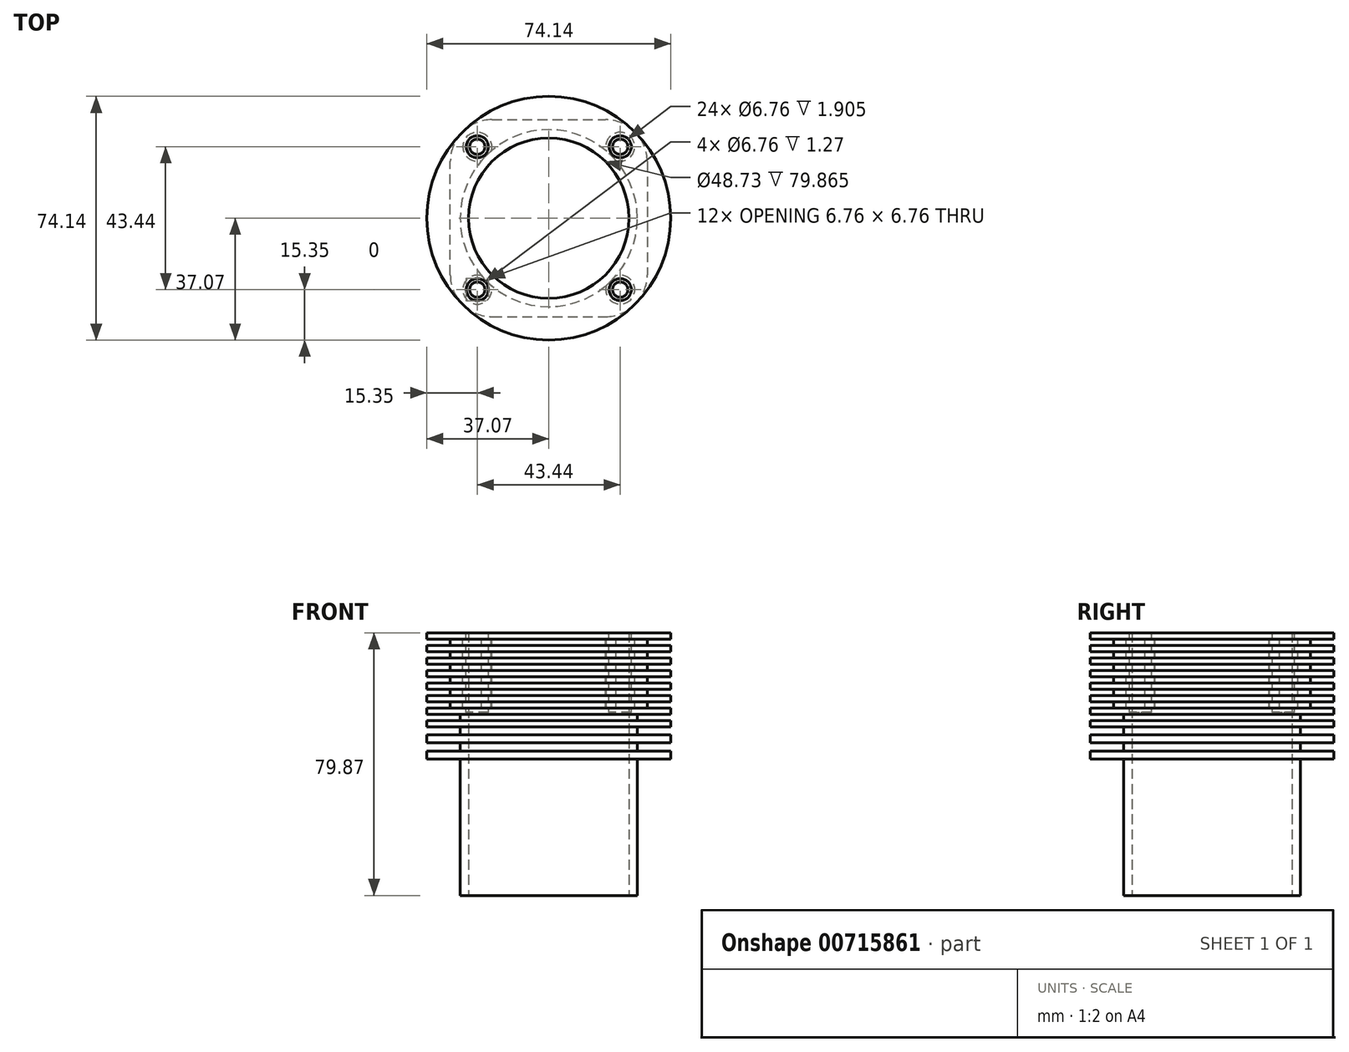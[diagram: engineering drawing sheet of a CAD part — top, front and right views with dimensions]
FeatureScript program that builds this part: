
annotation { "Feature Type Name" : "Feature", "Feature Type Description" : "" }
export const myFeature = defineFeature(function(context is Context, id is Id, definition is map)
    precondition{}
    {
        {
            var Q0;
            Q0=qCreatedBy(makeId("Front.planeOp"),FACE);
            var sketch = newSketch(context, id + "F0", { "sketchPlane" : qUnion([Q0])});
            skLineSegment(sketch, "E0", {"start": v(24.37, -35.45) * mm, "end": v(24.37, 44.42) * mm});
            skLineSegment(sketch, "E1", {"start": v(24.37, 44.42) * mm, "end": v(37.07, 44.42) * mm});
            skLineSegment(sketch, "E2", {"start": v(37.07, 42.51) * mm, "end": v(26.9, 42.51) * mm});
            skLineSegment(sketch, "E3", {"start": v(26.9, 42.51) * mm, "end": v(26.9, 40.6) * mm});
            skLineSegment(sketch, "E4", {"start": v(37.07, 42.51) * mm, "end": v(37.07, 44.42) * mm});
            skLineSegment(sketch, "E5", {"start": v(26.9, 40.6) * mm, "end": v(37.07, 40.6) * mm});
            skLineSegment(sketch, "E6", {"start": v(37.07, 40.6) * mm, "end": v(37.07, 38.7) * mm});
            skLineSegment(sketch, "E7", {"start": v(37.07, 38.7) * mm, "end": v(26.9, 38.7) * mm});
            skLineSegment(sketch, "E8", {"start": v(26.9, 38.7) * mm, "end": v(26.9, 36.8) * mm});
            skLineSegment(sketch, "E9", {"start": v(26.9, 36.8) * mm, "end": v(37.07, 36.8) * mm});
            skLineSegment(sketch, "E10", {"start": v(37.07, 36.8) * mm, "end": v(37.07, 34.9) * mm});
            skLineSegment(sketch, "E11", {"start": v(37.07, 34.9) * mm, "end": v(26.9, 34.9) * mm});
            skLineSegment(sketch, "E12", {"start": v(26.9, 34.9) * mm, "end": v(26.9, 32.99) * mm});
            skLineSegment(sketch, "E13", {"start": v(26.9, 32.99) * mm, "end": v(37.07, 32.99) * mm});
            skLineSegment(sketch, "E14", {"start": v(37.07, 32.99) * mm, "end": v(37.07, 31.08) * mm});
            skLineSegment(sketch, "E15", {"start": v(37.07, 31.08) * mm, "end": v(26.9, 31.08) * mm});
            skLineSegment(sketch, "E16", {"start": v(26.9, 31.08) * mm, "end": v(26.9, 29.18) * mm});
            skLineSegment(sketch, "E17", {"start": v(26.9, 29.18) * mm, "end": v(37.07, 29.18) * mm});
            skLineSegment(sketch, "E18", {"start": v(37.07, 29.18) * mm, "end": v(37.07, 27.27) * mm});
            skLineSegment(sketch, "E19", {"start": v(37.07, 27.27) * mm, "end": v(26.9, 27.27) * mm});
            skLineSegment(sketch, "E20", {"start": v(26.9, 27.27) * mm, "end": v(26.9, 25.37) * mm});
            skLineSegment(sketch, "E21", {"start": v(26.9, 25.37) * mm, "end": v(37.07, 25.37) * mm});
            skLineSegment(sketch, "E22", {"start": v(37.07, 25.37) * mm, "end": v(37.07, 23.46) * mm});
            skLineSegment(sketch, "E23", {"start": v(37.07, 23.46) * mm, "end": v(26.9, 23.46) * mm});
            skLineSegment(sketch, "E24", {"start": v(26.9, 23.46) * mm, "end": v(26.9, 21.56) * mm});
            skLineSegment(sketch, "E25", {"start": v(26.9, 21.56) * mm, "end": v(37.07, 21.56) * mm});
            skLineSegment(sketch, "E26", {"start": v(37.07, 21.56) * mm, "end": v(37.07, 19.65) * mm});
            skLineSegment(sketch, "E27", {"start": v(37.07, 19.65) * mm, "end": v(26.9, 19.65) * mm});
            skLineSegment(sketch, "E28", {"start": v(26.9, 19.65) * mm, "end": v(26.9, 17.75) * mm});
            skLineSegment(sketch, "E29", {"start": v(26.9, 17.75) * mm, "end": v(37.07, 17.75) * mm});
            skLineSegment(sketch, "E30", {"start": v(37.07, 17.75) * mm, "end": v(37.07, 15.84) * mm});
            skLineSegment(sketch, "E31", {"start": v(37.07, 15.84) * mm, "end": v(26.9, 15.84) * mm});
            skLineSegment(sketch, "E32", {"start": v(26.9, 15.84) * mm, "end": v(26.9, 13.38) * mm});
            skLineSegment(sketch, "E33", {"start": v(26.9, 13.38) * mm, "end": v(37.07, 13.38) * mm});
            skLineSegment(sketch, "E34", {"start": v(37.07, 13.38) * mm, "end": v(37.07, 10.93) * mm});
            skLineSegment(sketch, "E35", {"start": v(37.07, 10.93) * mm, "end": v(26.9, 10.93) * mm});
            skLineSegment(sketch, "E36", {"start": v(26.9, 10.93) * mm, "end": v(26.9, 8.47) * mm});
            skLineSegment(sketch, "E37", {"start": v(26.9, 8.47) * mm, "end": v(37.07, 8.47) * mm});
            skLineSegment(sketch, "E38", {"start": v(37.07, 8.47) * mm, "end": v(37.07, 6.02) * mm});
            skLineSegment(sketch, "E39", {"start": v(37.07, 6.02) * mm, "end": v(26.9, 6.02) * mm});
            skLineSegment(sketch, "E40", {"start": v(26.9, 6.02) * mm, "end": v(26.9, -35.45) * mm});
            skLineSegment(sketch, "E41", {"start": v(26.9, -35.45) * mm, "end": v(24.37, -35.45) * mm});
            skLineSegment(sketch, "E42", {"start": v(0, -13.6) * mm, "end": v(0, 23.15) * mm});
            skSolve(sketch);
        }
        {
            var Q0;
            Q0=makeQuery(id+"F0.imprint","IMPRINT",FACE,{"disambiguationData":[TD([[makeQuery(id+"F0.imprint","IMPRINT",EDGE,{"derivedFrom":sQuery(id+"F0.wireOp",EDGE,"E0")}),-1.0]])]});
            var Q1;
            Q1=sQuery(id+"F0.wireOp",EDGE,"E42");
            revolve(context, id + "F1", {"surfaceOperationType" : NewSurfaceOperationType.NEW, "entities" : qUnion([Q0]), "axis" : qUnion([Q1]), "revolveType" : RevolveType.FULL});
        }
        {
            var Q0;
            Q0=makeQuery(id+"F1.opRevolve","SWEPT_FACE",FACE,{"disambiguationData":[OSD([sQuery(id+"F0.wireOp",EDGE,"E1")])]});
            var sketch = newSketch(context, id + "F2", { "sketchPlane" : qUnion([Q0])});
            skLineSegment(sketch, "E43.bottom", {"start": v(17.23, 29.93) * mm, "end": v(-17.23, 29.93) * mm});
            skLineSegment(sketch, "E43.top", {"start": v(17.23, -29.93) * mm, "end": v(-17.23, -29.93) * mm});
            skLineSegment(sketch, "E43.left", {"start": v(29.93, 17.23) * mm, "end": v(29.93, -17.23) * mm});
            skLineSegment(sketch, "E43.right", {"start": v(-29.93, 17.23) * mm, "end": v(-29.93, -17.23) * mm});
            skPoint(sketch, "E43.middle", {"position": v(0, 0) * mm});
            skPoint(sketch, "E44.visualSharp", {"position": v(-29.93, 29.93) * mm});
            skArc(sketch, "E44.filletArc", {"start": v(-17.23, 29.93) * mm, "mid": v(-26.21, 26.21) * mm, "end": v(-29.93, 17.23) * mm});
            skPoint(sketch, "E45.visualSharp", {"position": v(29.93, 29.93) * mm});
            skArc(sketch, "E45.filletArc", {"start": v(29.93, 17.23) * mm, "mid": v(26.21, 26.21) * mm, "end": v(17.23, 29.93) * mm});
            skPoint(sketch, "E46.visualSharp", {"position": v(29.93, -29.93) * mm});
            skArc(sketch, "E46.filletArc", {"start": v(17.23, -29.93) * mm, "mid": v(26.21, -26.21) * mm, "end": v(29.93, -17.23) * mm});
            skPoint(sketch, "E47.visualSharp", {"position": v(-29.93, -29.93) * mm});
            skArc(sketch, "E47.filletArc", {"start": v(-29.93, -17.23) * mm, "mid": v(-26.21, -26.21) * mm, "end": v(-17.23, -29.93) * mm});
            skCircle(sketch, "E48", {"center": v(-21.72, 21.72) * mm, "radius": 4.41 * mm});
            skCircle(sketch, "E49.MirrorC", {"center": v(21.72, 21.72) * mm, "radius": 4.41 * mm});
            skCircle(sketch, "E50.MirrorC", {"center": v(-21.72, -21.72) * mm, "radius": 4.41 * mm});
            skCircle(sketch, "E51.MirrorC", {"center": v(21.72, -21.72) * mm, "radius": 4.41 * mm});
            skSolve(sketch);
        }
        {
            var Q0;
            {var subQ7=sQuery(id+"F2.wireOp",EDGE,"E43.bottom");Q0=makeQuery(id+"F2.imprint","IMPRINT",FACE,{"disambiguationData":[TD([[makeQuery(id+"F2.imprint","IMPRINT",EDGE,{"derivedFrom":subQ7}),1.0]])]});}
            extrude(context, id + "F3", {"entities" : qUnion([Q0]), "operationType" : NewBodyOperationType.ADD, "oppositeDirection" : true, "depth" : 24.13 * mm, "offsetDistance" : 25.4 * mm});
        }
        {
            var Q0;
            Q0=sQuery(id+"F2.wireOp",VERTEX,"E50.MirrorC.center");
            var Q1;
            Q1=makeQuery(id+"F1.opRevolve","SWEPT_BODY",BODY,{"disambiguationData":[OSD([sQuery(id+"F0.wireOp",EDGE,"E0"),sQuery(id+"F0.wireOp",EDGE,"E1"),sQuery(id+"F0.wireOp",EDGE,"E2"),sQuery(id+"F0.wireOp",EDGE,"E3"),sQuery(id+"F0.wireOp",EDGE,"E4"),sQuery(id+"F0.wireOp",EDGE,"E5"),sQuery(id+"F0.wireOp",EDGE,"E6"),sQuery(id+"F0.wireOp",EDGE,"E7"),sQuery(id+"F0.wireOp",EDGE,"E8"),sQuery(id+"F0.wireOp",EDGE,"E9"),sQuery(id+"F0.wireOp",EDGE,"E10"),sQuery(id+"F0.wireOp",EDGE,"E11"),sQuery(id+"F0.wireOp",EDGE,"E12"),sQuery(id+"F0.wireOp",EDGE,"E13"),sQuery(id+"F0.wireOp",EDGE,"E14"),sQuery(id+"F0.wireOp",EDGE,"E15"),sQuery(id+"F0.wireOp",EDGE,"E16"),sQuery(id+"F0.wireOp",EDGE,"E17"),sQuery(id+"F0.wireOp",EDGE,"E18"),sQuery(id+"F0.wireOp",EDGE,"E19"),sQuery(id+"F0.wireOp",EDGE,"E20"),sQuery(id+"F0.wireOp",EDGE,"E21"),sQuery(id+"F0.wireOp",EDGE,"E22"),sQuery(id+"F0.wireOp",EDGE,"E23"),sQuery(id+"F0.wireOp",EDGE,"E24"),sQuery(id+"F0.wireOp",EDGE,"E25"),sQuery(id+"F0.wireOp",EDGE,"E26"),sQuery(id+"F0.wireOp",EDGE,"E27"),sQuery(id+"F0.wireOp",EDGE,"E28"),sQuery(id+"F0.wireOp",EDGE,"E29"),sQuery(id+"F0.wireOp",EDGE,"E30"),sQuery(id+"F0.wireOp",EDGE,"E31"),sQuery(id+"F0.wireOp",EDGE,"E32"),sQuery(id+"F0.wireOp",EDGE,"E33"),sQuery(id+"F0.wireOp",EDGE,"E34"),sQuery(id+"F0.wireOp",EDGE,"E35"),sQuery(id+"F0.wireOp",EDGE,"E36"),sQuery(id+"F0.wireOp",EDGE,"E37"),sQuery(id+"F0.wireOp",EDGE,"E38"),sQuery(id+"F0.wireOp",EDGE,"E39"),sQuery(id+"F0.wireOp",EDGE,"E40"),sQuery(id+"F0.wireOp",EDGE,"E41")])]});
            hole(context, id + "F4", {"style" : HoleStyle.SIMPLE, "endStyle" : HoleEndStyle.BLIND, "standardTappedOrClearance" : lookupTablePath({ "standard" : "ANSI", "fit" : "Normal (ASME)", "size" : "1/4", "type" : "Clearance" }), "standardBlindInLast" : lookupTablePath({ "fit" : "Free", "standard" : "ANSI", "size" : "1/4", "type" : "Clearance" }), "holeDiameter" : 6.76 * mm, "majorDiameter" : 6.35 * mm, "holeDepth" : 24.13 * mm, "isTappedThrough" : true, "tappedDepth" : 12.7 * mm, "tapClearance" : 3, "startFromSketch" : true, "locations" : qUnion([Q0]), "scope" : qUnion([Q1])});
        }
        {
            var Q0;
            Q0=sQuery(id+"F2.wireOp",VERTEX,"E51.MirrorC.center");
            var Q1;
            Q1=makeQuery(id+"F1.opRevolve","SWEPT_BODY",BODY,{"disambiguationData":[OSD([sQuery(id+"F0.wireOp",EDGE,"E0"),sQuery(id+"F0.wireOp",EDGE,"E1"),sQuery(id+"F0.wireOp",EDGE,"E2"),sQuery(id+"F0.wireOp",EDGE,"E3"),sQuery(id+"F0.wireOp",EDGE,"E4"),sQuery(id+"F0.wireOp",EDGE,"E5"),sQuery(id+"F0.wireOp",EDGE,"E6"),sQuery(id+"F0.wireOp",EDGE,"E7"),sQuery(id+"F0.wireOp",EDGE,"E8"),sQuery(id+"F0.wireOp",EDGE,"E9"),sQuery(id+"F0.wireOp",EDGE,"E10"),sQuery(id+"F0.wireOp",EDGE,"E11"),sQuery(id+"F0.wireOp",EDGE,"E12"),sQuery(id+"F0.wireOp",EDGE,"E13"),sQuery(id+"F0.wireOp",EDGE,"E14"),sQuery(id+"F0.wireOp",EDGE,"E15"),sQuery(id+"F0.wireOp",EDGE,"E16"),sQuery(id+"F0.wireOp",EDGE,"E17"),sQuery(id+"F0.wireOp",EDGE,"E18"),sQuery(id+"F0.wireOp",EDGE,"E19"),sQuery(id+"F0.wireOp",EDGE,"E20"),sQuery(id+"F0.wireOp",EDGE,"E21"),sQuery(id+"F0.wireOp",EDGE,"E22"),sQuery(id+"F0.wireOp",EDGE,"E23"),sQuery(id+"F0.wireOp",EDGE,"E24"),sQuery(id+"F0.wireOp",EDGE,"E25"),sQuery(id+"F0.wireOp",EDGE,"E26"),sQuery(id+"F0.wireOp",EDGE,"E27"),sQuery(id+"F0.wireOp",EDGE,"E28"),sQuery(id+"F0.wireOp",EDGE,"E29"),sQuery(id+"F0.wireOp",EDGE,"E30"),sQuery(id+"F0.wireOp",EDGE,"E31"),sQuery(id+"F0.wireOp",EDGE,"E32"),sQuery(id+"F0.wireOp",EDGE,"E33"),sQuery(id+"F0.wireOp",EDGE,"E34"),sQuery(id+"F0.wireOp",EDGE,"E35"),sQuery(id+"F0.wireOp",EDGE,"E36"),sQuery(id+"F0.wireOp",EDGE,"E37"),sQuery(id+"F0.wireOp",EDGE,"E38"),sQuery(id+"F0.wireOp",EDGE,"E39"),sQuery(id+"F0.wireOp",EDGE,"E40"),sQuery(id+"F0.wireOp",EDGE,"E41")])]});
            hole(context, id + "F5", {"style" : HoleStyle.SIMPLE, "endStyle" : HoleEndStyle.BLIND, "standardTappedOrClearance" : lookupTablePath({ "standard" : "ANSI", "fit" : "Normal (ASME)", "size" : "1/4", "type" : "Clearance" }), "standardBlindInLast" : lookupTablePath({ "fit" : "Free", "standard" : "ANSI", "size" : "1/4", "type" : "Clearance" }), "holeDiameter" : 6.76 * mm, "majorDiameter" : 6.35 * mm, "holeDepth" : 24.13 * mm, "isTappedThrough" : true, "tappedDepth" : 12.7 * mm, "tapClearance" : 3, "startFromSketch" : true, "locations" : qUnion([Q0]), "scope" : qUnion([Q1])});
        }
        {
            var Q0;
            Q0=sQuery(id+"F2.wireOp",VERTEX,"E49.MirrorC.center");
            var Q1;
            Q1=makeQuery(id+"F1.opRevolve","SWEPT_BODY",BODY,{"disambiguationData":[OSD([sQuery(id+"F0.wireOp",EDGE,"E0"),sQuery(id+"F0.wireOp",EDGE,"E1"),sQuery(id+"F0.wireOp",EDGE,"E2"),sQuery(id+"F0.wireOp",EDGE,"E3"),sQuery(id+"F0.wireOp",EDGE,"E4"),sQuery(id+"F0.wireOp",EDGE,"E5"),sQuery(id+"F0.wireOp",EDGE,"E6"),sQuery(id+"F0.wireOp",EDGE,"E7"),sQuery(id+"F0.wireOp",EDGE,"E8"),sQuery(id+"F0.wireOp",EDGE,"E9"),sQuery(id+"F0.wireOp",EDGE,"E10"),sQuery(id+"F0.wireOp",EDGE,"E11"),sQuery(id+"F0.wireOp",EDGE,"E12"),sQuery(id+"F0.wireOp",EDGE,"E13"),sQuery(id+"F0.wireOp",EDGE,"E14"),sQuery(id+"F0.wireOp",EDGE,"E15"),sQuery(id+"F0.wireOp",EDGE,"E16"),sQuery(id+"F0.wireOp",EDGE,"E17"),sQuery(id+"F0.wireOp",EDGE,"E18"),sQuery(id+"F0.wireOp",EDGE,"E19"),sQuery(id+"F0.wireOp",EDGE,"E20"),sQuery(id+"F0.wireOp",EDGE,"E21"),sQuery(id+"F0.wireOp",EDGE,"E22"),sQuery(id+"F0.wireOp",EDGE,"E23"),sQuery(id+"F0.wireOp",EDGE,"E24"),sQuery(id+"F0.wireOp",EDGE,"E25"),sQuery(id+"F0.wireOp",EDGE,"E26"),sQuery(id+"F0.wireOp",EDGE,"E27"),sQuery(id+"F0.wireOp",EDGE,"E28"),sQuery(id+"F0.wireOp",EDGE,"E29"),sQuery(id+"F0.wireOp",EDGE,"E30"),sQuery(id+"F0.wireOp",EDGE,"E31"),sQuery(id+"F0.wireOp",EDGE,"E32"),sQuery(id+"F0.wireOp",EDGE,"E33"),sQuery(id+"F0.wireOp",EDGE,"E34"),sQuery(id+"F0.wireOp",EDGE,"E35"),sQuery(id+"F0.wireOp",EDGE,"E36"),sQuery(id+"F0.wireOp",EDGE,"E37"),sQuery(id+"F0.wireOp",EDGE,"E38"),sQuery(id+"F0.wireOp",EDGE,"E39"),sQuery(id+"F0.wireOp",EDGE,"E40"),sQuery(id+"F0.wireOp",EDGE,"E41")])]});
            hole(context, id + "F6", {"style" : HoleStyle.SIMPLE, "endStyle" : HoleEndStyle.BLIND, "standardTappedOrClearance" : lookupTablePath({ "standard" : "ANSI", "fit" : "Normal (ASME)", "size" : "1/4", "type" : "Clearance" }), "standardBlindInLast" : lookupTablePath({ "fit" : "Free", "standard" : "ANSI", "size" : "1/4", "type" : "Clearance" }), "holeDiameter" : 6.76 * mm, "majorDiameter" : 6.35 * mm, "holeDepth" : 24.13 * mm, "isTappedThrough" : true, "tappedDepth" : 12.7 * mm, "tapClearance" : 3, "startFromSketch" : true, "locations" : qUnion([Q0]), "scope" : qUnion([Q1])});
        }
        {
            var Q0;
            Q0=sQuery(id+"F2.wireOp",VERTEX,"E48.center");
            var Q1;
            Q1=makeQuery(id+"F1.opRevolve","SWEPT_BODY",BODY,{"disambiguationData":[OSD([sQuery(id+"F0.wireOp",EDGE,"E0"),sQuery(id+"F0.wireOp",EDGE,"E1"),sQuery(id+"F0.wireOp",EDGE,"E2"),sQuery(id+"F0.wireOp",EDGE,"E3"),sQuery(id+"F0.wireOp",EDGE,"E4"),sQuery(id+"F0.wireOp",EDGE,"E5"),sQuery(id+"F0.wireOp",EDGE,"E6"),sQuery(id+"F0.wireOp",EDGE,"E7"),sQuery(id+"F0.wireOp",EDGE,"E8"),sQuery(id+"F0.wireOp",EDGE,"E9"),sQuery(id+"F0.wireOp",EDGE,"E10"),sQuery(id+"F0.wireOp",EDGE,"E11"),sQuery(id+"F0.wireOp",EDGE,"E12"),sQuery(id+"F0.wireOp",EDGE,"E13"),sQuery(id+"F0.wireOp",EDGE,"E14"),sQuery(id+"F0.wireOp",EDGE,"E15"),sQuery(id+"F0.wireOp",EDGE,"E16"),sQuery(id+"F0.wireOp",EDGE,"E17"),sQuery(id+"F0.wireOp",EDGE,"E18"),sQuery(id+"F0.wireOp",EDGE,"E19"),sQuery(id+"F0.wireOp",EDGE,"E20"),sQuery(id+"F0.wireOp",EDGE,"E21"),sQuery(id+"F0.wireOp",EDGE,"E22"),sQuery(id+"F0.wireOp",EDGE,"E23"),sQuery(id+"F0.wireOp",EDGE,"E24"),sQuery(id+"F0.wireOp",EDGE,"E25"),sQuery(id+"F0.wireOp",EDGE,"E26"),sQuery(id+"F0.wireOp",EDGE,"E27"),sQuery(id+"F0.wireOp",EDGE,"E28"),sQuery(id+"F0.wireOp",EDGE,"E29"),sQuery(id+"F0.wireOp",EDGE,"E30"),sQuery(id+"F0.wireOp",EDGE,"E31"),sQuery(id+"F0.wireOp",EDGE,"E32"),sQuery(id+"F0.wireOp",EDGE,"E33"),sQuery(id+"F0.wireOp",EDGE,"E34"),sQuery(id+"F0.wireOp",EDGE,"E35"),sQuery(id+"F0.wireOp",EDGE,"E36"),sQuery(id+"F0.wireOp",EDGE,"E37"),sQuery(id+"F0.wireOp",EDGE,"E38"),sQuery(id+"F0.wireOp",EDGE,"E39"),sQuery(id+"F0.wireOp",EDGE,"E40"),sQuery(id+"F0.wireOp",EDGE,"E41")])]});
            hole(context, id + "F7", {"style" : HoleStyle.SIMPLE, "endStyle" : HoleEndStyle.BLIND, "standardTappedOrClearance" : lookupTablePath({ "standard" : "ANSI", "fit" : "Normal (ASME)", "size" : "1/4", "type" : "Clearance" }), "standardBlindInLast" : lookupTablePath({ "fit" : "Free", "standard" : "ANSI", "size" : "1/4", "type" : "Clearance" }), "holeDiameter" : 6.76 * mm, "majorDiameter" : 6.35 * mm, "holeDepth" : 24.13 * mm, "isTappedThrough" : true, "tappedDepth" : 12.7 * mm, "tapClearance" : 3, "startFromSketch" : true, "locations" : qUnion([Q0]), "scope" : qUnion([Q1])});
        }
    });
